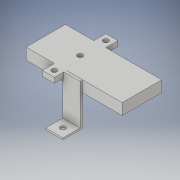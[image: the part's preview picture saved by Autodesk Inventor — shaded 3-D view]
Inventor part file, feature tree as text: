
AUTODESK INVENTOR PART (.ipt)
format: ipt  version: 2018 (Build 220112000, 112)  size: 194,560 bytes
history: native  units: in
note: dims shown in document units (in); Inventor stores cm internally (conversion verified against a paired STEP export)
features: extrude x9, sketch x9
ambient origin geometry x8: Origin, YZ Plane, XZ Plane, XY Plane, X Axis, Y Axis, Z Axis, Center Point
bodies: Solid1 (feature_tree)
feature tree (18):
  extrude  "Extrusion1"  Depth=0.3937in
  extrude  "Extrusion2"  Depth=0.0394in TaperAngle=0.0deg
  extrude  "Extrusion3"  Depth=0.0394in TaperAngle=0.0deg
  extrude  "Extrusion4"  Depth=0.6693in TaperAngle=0.0deg
  extrude  "Extrusion5"  TaperAngle=0.0deg  [1 undecoded]
  extrude  "Extrusion6"  Depth=2.2047in
  extrude  "Extrusion7"  Depth=0.9055in
  extrude  "Extrusion8"  Depth=0.1969in TaperAngle=0.0deg
  extrude  "Extrusion9"  Depth=0.2756in
  sketch  "Sketch1"  dims[d0=0.3937in d1=0.3937in]
  sketch  "Sketch2"  dims[d2=0.1181in d3=0.0394in d4=0.0in]
  sketch  "Sketch3"  dims[d5=0.0591in d6=0.0394in d7=0.0in]
  sketch  "Sketch4"  dims[d8=0.0591in d9=0.6693in d10=0.0in]
  sketch  "Sketch5"  dims[d11=0.0591in d12=0.0in d13=0.0in]
  sketch  "Sketch6"  dims[d14=0.0591in d15=2.2047in]
  sketch  "Sketch8"  dims[d16=0.9055in d17=0.0in d18=0.7874in]
  sketch  "Sketch9"  dims[d19=0.1181in d20=0.1969in d21=0.0in]
  sketch  "Sketch10"  dims[d27=0.1181in d28=0.0in d29=0.7874in d30=0.0in d31=0.2756in d32=0.2756in d33=0.0in d34=0.2756in d35=0.2756in d36=0.1181in d37=0.1181in d38=0.1969in d39=0.0in d40=0.2756in d41=0.0in]
note: 1 required parameter value undecoded (feature->parameter linkage not recoverable at this tier; creation-order binding heuristic only, values carry confidence <= 0.55)
